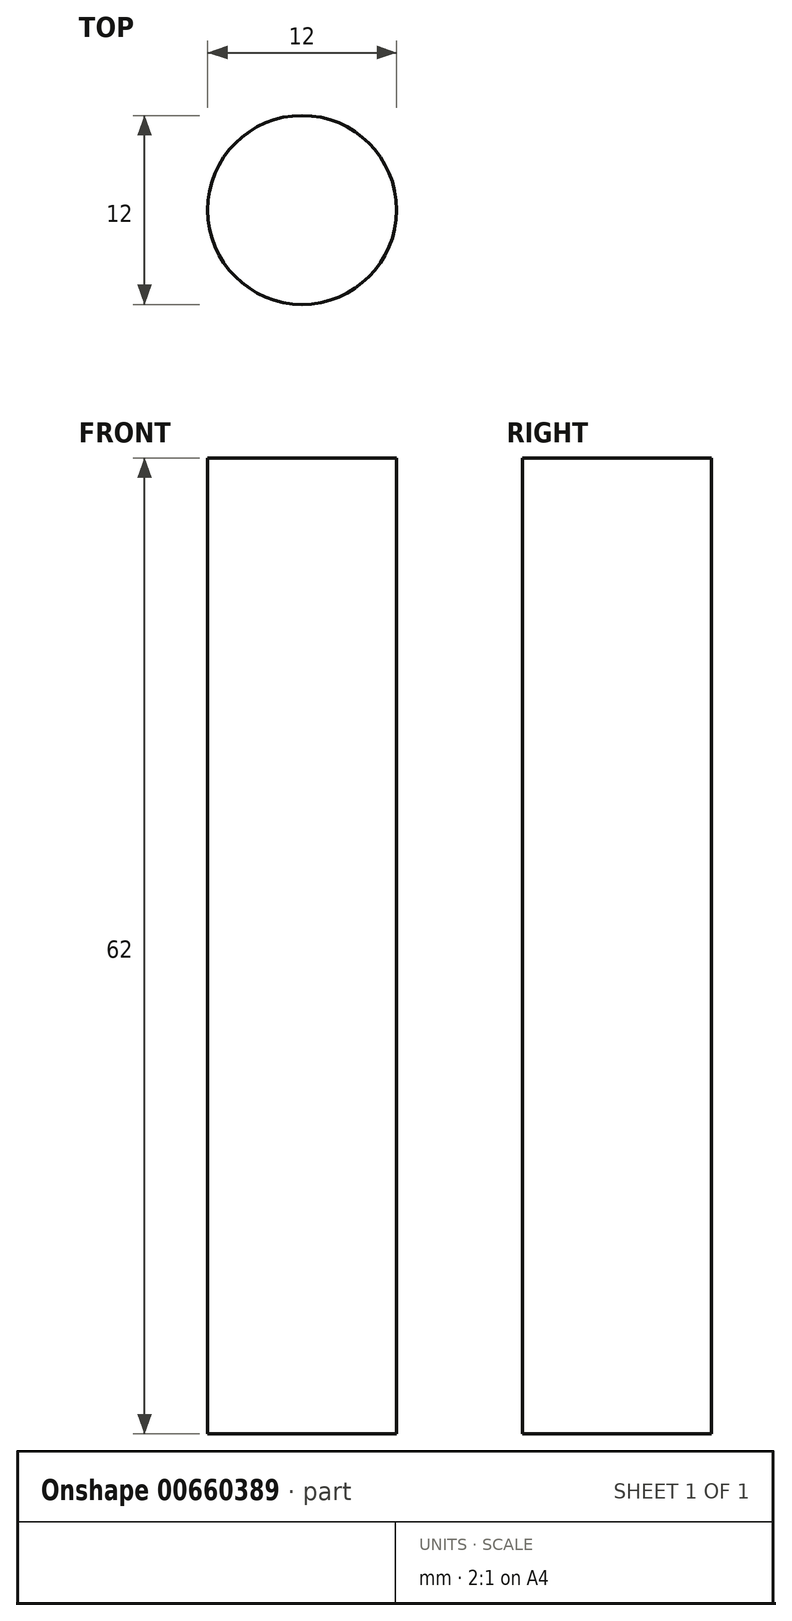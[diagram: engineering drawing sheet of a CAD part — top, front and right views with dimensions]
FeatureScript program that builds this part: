
annotation { "Feature Type Name" : "Feature", "Feature Type Description" : "" }
export const myFeature = defineFeature(function(context is Context, id is Id, definition is map)
    precondition{}
    {
        {
            var Q0;
            Q0=qCreatedBy(makeId("Top.planeOp"),FACE);
            var sketch = newSketch(context, id + "F0", { "sketchPlane" : qUnion([Q0])});
            skCircle(sketch, "E0", {"center": v(0, 0) * mm, "radius": 6 * mm});
            skSolve(sketch);
        }
        {
            var Q0;
            Q0=makeQuery(id+"F0.imprint","IMPRINT",FACE,{"disambiguationData":[TD([[makeQuery(id+"F0.imprint","IMPRINT",EDGE,{"derivedFrom":sQuery(id+"F0.wireOp",EDGE,"E0")}),1.0]])]});
            extrude(context, id + "F1", {"entities" : qUnion([Q0]), "depth" : 62 * mm, "offsetDistance" : 25 * mm});
        }
    });
